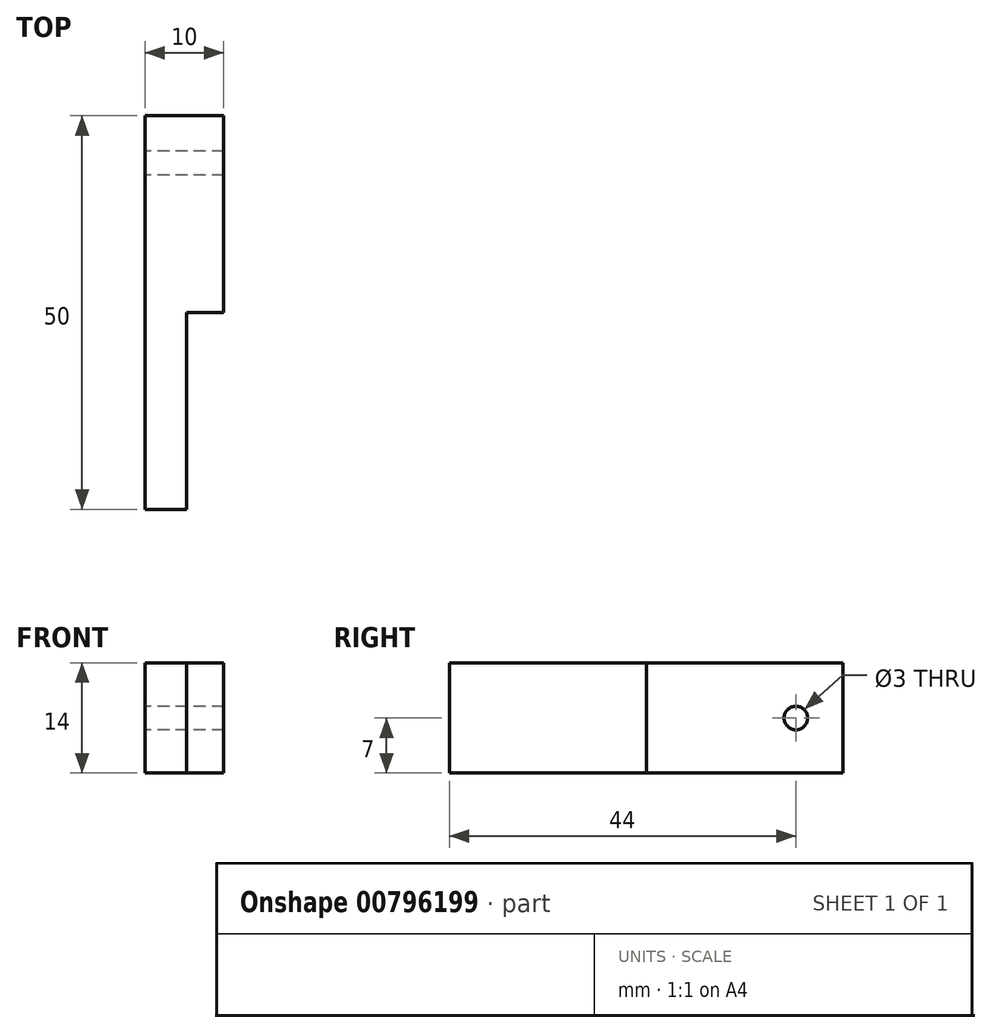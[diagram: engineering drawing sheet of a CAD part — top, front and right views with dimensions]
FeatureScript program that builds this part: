
annotation { "Feature Type Name" : "Feature", "Feature Type Description" : "" }
export const myFeature = defineFeature(function(context is Context, id is Id, definition is map)
    precondition{}
    {
        {
            var Q0;
            Q0=qCreatedBy(makeId("Top.planeOp"),FACE);
            var sketch = newSketch(context, id + "F0", { "sketchPlane" : qUnion([Q0])});
            skLineSegment(sketch, "E0.bottom", {"start": v(5, -25) * mm, "end": v(-5, -25) * mm});
            skLineSegment(sketch, "E0.top", {"start": v(5, 25) * mm, "end": v(-5, 25) * mm});
            skLineSegment(sketch, "E0.left", {"start": v(5, -25) * mm, "end": v(5, 25) * mm});
            skLineSegment(sketch, "E0.right", {"start": v(-5, -25) * mm, "end": v(-5, 25) * mm});
            skPoint(sketch, "E0.middle", {"position": v(0, 0) * mm});
            skLineSegment(sketch, "E1.bottom", {"start": v(5, -25) * mm, "end": v(0.25, -25) * mm});
            skLineSegment(sketch, "E1.top", {"start": v(5, 0) * mm, "end": v(0.25, 0) * mm});
            skLineSegment(sketch, "E1.left", {"start": v(5, -25) * mm, "end": v(5, 0) * mm});
            skLineSegment(sketch, "E1.right", {"start": v(0.25, -25) * mm, "end": v(0.25, 0) * mm});
            skSolve(sketch);
        }
        {
            var Q0;
            {var subQ1=sQuery(id+"F0.wireOp",EDGE,"E0.top");Q0=makeQuery(id+"F0.imprint","IMPRINT",FACE,{"disambiguationData":[TD([[makeQuery(id+"F0.imprint","IMPRINT",EDGE,{"derivedFrom":subQ1}),1.0]])]});}
            extrude(context, id + "F1", {"entities" : qUnion([Q0]), "depth" : 14 * mm, "offsetDistance" : 25 * mm});
        }
        {
            var Q0;
            Q0=makeQuery(id+"F1.opExtrude","SWEPT_FACE",FACE,{"disambiguationData":[OSD([sQuery(id+"F0.wireOp",EDGE,"E0.right")])]});
            var sketch = newSketch(context, id + "F2", { "sketchPlane" : qUnion([Q0])});
            skCircle(sketch, "E2", {"center": v(-19, 7) * mm, "radius": 1.5 * mm});
            skPoint(sketch, "E2.centerSnap0", {"position": v(-25, 7) * mm});
            skSolve(sketch);
        }
        {
            var Q0;
            Q0=makeQuery(id+"F2.imprint","IMPRINT",FACE,{"disambiguationData":[TD([[makeQuery(id+"F2.imprint","IMPRINT",EDGE,{"derivedFrom":sQuery(id+"F2.wireOp",EDGE,"E2")}),1.0]])]});
            extrude(context, id + "F3", {"entities" : qUnion([Q0]), "operationType" : NewBodyOperationType.REMOVE, "oppositeDirection" : true, "depth" : 25 * mm, "offsetDistance" : 25 * mm});
        }
    });
